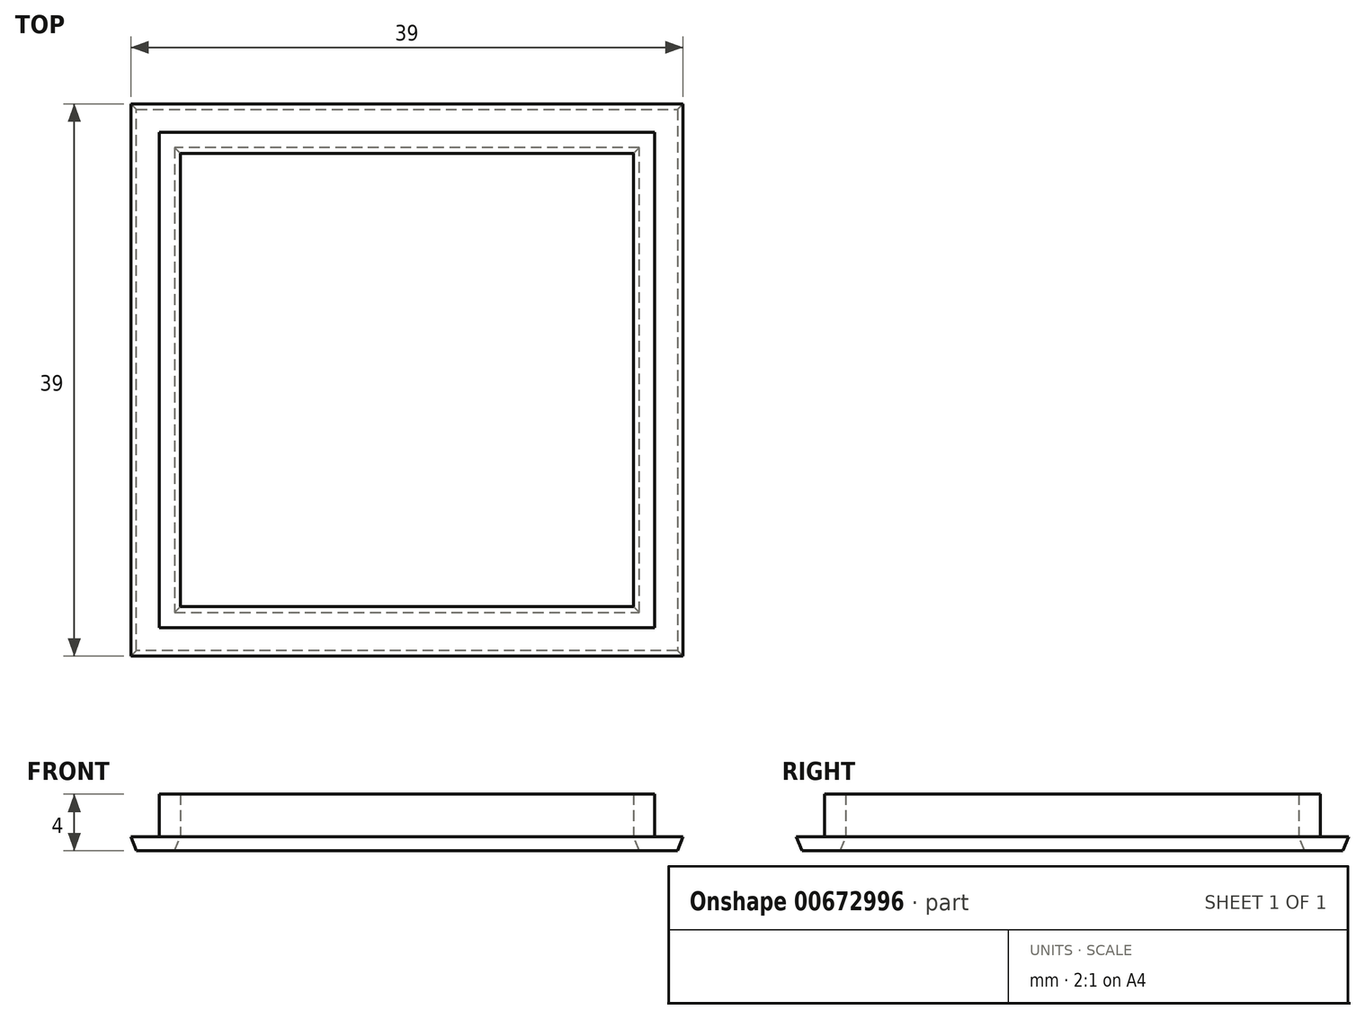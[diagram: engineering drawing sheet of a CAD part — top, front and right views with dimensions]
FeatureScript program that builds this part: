
annotation { "Feature Type Name" : "Feature", "Feature Type Description" : "" }
export const myFeature = defineFeature(function(context is Context, id is Id, definition is map)
    precondition{}
    {
        {
            var Q0;
            Q0=qCreatedBy(makeId("Top.planeOp"),FACE);
            var sketch = newSketch(context, id + "F0", { "sketchPlane" : qUnion([Q0])});
            skLineSegment(sketch, "E0.bottom", {"start": v(16, -16) * mm, "end": v(-16, -16) * mm});
            skLineSegment(sketch, "E0.top", {"start": v(16, 16) * mm, "end": v(-16, 16) * mm});
            skLineSegment(sketch, "E0.left", {"start": v(16, -16) * mm, "end": v(16, 16) * mm});
            skLineSegment(sketch, "E0.right", {"start": v(-16, -16) * mm, "end": v(-16, 16) * mm});
            skPoint(sketch, "E0.middle", {"position": v(0, 0) * mm});
            skLineSegment(sketch, "E1.bottom", {"start": v(17.5, -17.5) * mm, "end": v(-17.5, -17.5) * mm});
            skLineSegment(sketch, "E1.top", {"start": v(17.5, 17.5) * mm, "end": v(-17.5, 17.5) * mm});
            skLineSegment(sketch, "E1.left", {"start": v(17.5, -17.5) * mm, "end": v(17.5, 17.5) * mm});
            skLineSegment(sketch, "E1.right", {"start": v(-17.5, -17.5) * mm, "end": v(-17.5, 17.5) * mm});
            skLineSegment(sketch, "E2.bottom", {"start": v(19.5, -19.5) * mm, "end": v(-19.5, -19.5) * mm});
            skLineSegment(sketch, "E2.top", {"start": v(19.5, 19.5) * mm, "end": v(-19.5, 19.5) * mm});
            skLineSegment(sketch, "E2.left", {"start": v(19.5, -19.5) * mm, "end": v(19.5, 19.5) * mm});
            skLineSegment(sketch, "E2.right", {"start": v(-19.5, -19.5) * mm, "end": v(-19.5, 19.5) * mm});
            skSolve(sketch);
        }
        {
            var Q0;
            Q0=makeQuery(id+"F0.imprint","IMPRINT",FACE,{"disambiguationData":[TD([[makeQuery(id+"F0.imprint","IMPRINT",EDGE,{"derivedFrom":sQuery(id+"F0.wireOp",EDGE,"E0.bottom")}),1.0]])]});
            extrude(context, id + "F1", {"entities" : qUnion([Q0]), "depth" : 4 * mm, "offsetDistance" : 25 * mm});
        }
        {
            var Q0;
            Q0=makeQuery(id+"F0.imprint","IMPRINT",FACE,{"disambiguationData":[TD([[makeQuery(id+"F0.imprint","IMPRINT",EDGE,{"derivedFrom":sQuery(id+"F0.wireOp",EDGE,"E1.bottom")}),1.0]])]});
            extrude(context, id + "F2", {"entities" : qUnion([Q0]), "operationType" : NewBodyOperationType.ADD, "depth" : 1 * mm, "offsetDistance" : 25 * mm});
        }
        {
            var Q0;
            {var subQ0=sQuery(id+"F0.wireOp",EDGE,"E1.right");var subQ1=sQuery(id+"F0.wireOp",EDGE,"E1.left");var subQ2=sQuery(id+"F0.wireOp",EDGE,"E1.top");var subQ3=sQuery(id+"F0.wireOp",EDGE,"E1.bottom");Q0=makeQuery(id+"F2.boolean.opBoolean","MERGE",FACE,{"derivedFrom":[makeQuery(id+"F1.opExtrude","CAP_FACE",FACE,{"disambiguationData":[OSD([sQuery(id+"F0.wireOp",EDGE,"E0.bottom"),sQuery(id+"F0.wireOp",EDGE,"E0.top"),sQuery(id+"F0.wireOp",EDGE,"E0.left"),sQuery(id+"F0.wireOp",EDGE,"E0.right"),subQ3,subQ2,subQ1,subQ0])],"isStart":true}),makeQuery(id+"F2.opExtrude","CAP_FACE",FACE,{"disambiguationData":[OSD([subQ3,subQ2,subQ1,subQ0,sQuery(id+"F0.wireOp",EDGE,"E2.bottom"),sQuery(id+"F0.wireOp",EDGE,"E2.top"),sQuery(id+"F0.wireOp",EDGE,"E2.left"),sQuery(id+"F0.wireOp",EDGE,"E2.right")])],"isStart":true})]});}
            chamfer(context, id + "F3", {"entities" : qUnion([Q0]), "chamferType" : ChamferType.TWO_OFFSETS, "width1" : 1 * mm, "oppositeDirection" : false, "width2" : 0.4 * mm, "tangentPropagation" : true});
        }
    });
